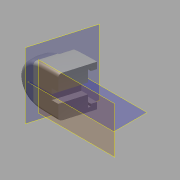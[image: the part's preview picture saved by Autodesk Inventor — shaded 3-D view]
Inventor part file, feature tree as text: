
AUTODESK INVENTOR PART (.ipt)
format: ipt  version: 2012 SP2 (Build 160219200, 219)  size: 716,288 bytes
history: native  units: in
note: dims shown in document units (in); Inventor stores cm internally (conversion verified against a paired STEP export)
features: sketch x21, sweep x7, extrude x5, plane x4, projected_geometry x3, fillet x2, other x2, mirror x1, surface_op x1
ambient origin geometry x8: Origin, YZ Plane, XZ Plane, XY Plane, X Axis, Y Axis, Z Axis, Center Point
bodies: Solid1 (feature_tree)
feature tree (46):
  sketch  "Sketch1"  dims[d6=0.9405in d9=0.688in]
  plane  "Work Plane1"
  plane  "Work Plane2"
  sketch  "Sketch3"  dims[d12=0.2381in d13=0.5734in]
  plane  "Work Plane3"
  sweep  "Sweep1"
  sweep  "Sweep2"
  extrude  "Extrusion1"  Depth=0.5734in
  plane  "Work Plane4"
  mirror  "Mirror1"
  sweep  "Sweep3"
  sweep  "Sweep5"
  sweep  "Sweep6"
  extrude  "Extrusion3"  Depth=0.7769in
  fillet  "Fillet2"  Radius=0.3374in
  fillet  "Fillet3"  Radius=0.1206in
  sweep  "Sweep8"
  sweep  "Sweep9"
  extrude  "Extrusion4"  Depth=0.9887in
  extrude  "Extrusion5"  Depth=1.1563in
  extrude  "Extrusion6"  Depth=1.2792in
  other  "Image1"
  sketch  "Sketch2"  dims[d10=0.069in d11=0.12in]
  other  "Srf1"
  sketch  "Sketch4"  dims[d14=0.4256in d15=1.588in]
  sketch  "Sketch5"  dims[d16=0.3503in d17=0.5806in]
  sketch  "Sketch6"  dims[d18=0.3426in d19=0.2058in]
  sketch  "Sketch7"  dims[d20=0.3395in d21=0.7769in d22=0.3374in d23=0.1206in]
  sketch  "Sketch8"  dims[d24=0.3329in d25=0.8673in]
  sketch  "Sketch9"  dims[d26=0.3313in d27=0.0621in]
  sketch  "Sketch10"  dims[d28=0.323in d29=0.9887in]
  sketch  "Sketch14"  dims[d30=0.2944in d31=1.1563in]
  sketch  "Sketch15"  dims[d32=0.2583in d33=1.2792in]
  sketch  "Sketch16"  dims[d34=0.1988in]
  sketch  "Sketch18"  dims[d35=1.391in]
  projected_geometry  "Projected Loop2"
  sketch  "Sketch20"  dims[d36=0.1269in]
  sketch  "3D Sketch2"
  sketch  "Sketch21"  dims[d37=1.4752in]
  sketch  "3D Sketch3"
  sketch  "Sketch22"  dims[d38=0.0171in]
  projected_geometry  "Projected Loop3"
  projected_geometry  "Projected Loop4"
  sketch  "Sketch23"  dims[d39=1.5524in]
  sketch  "Sketch24"  dims[d40=0.0519in d41=1.5805in d42=0.1042in d43=1.7561in d44=0.2965in d47=0.5902in d48=0.2in d49=0.0in d50=0.6495in d51=1.035in d52=0.5105in d53=0.306in d54=0.5955in d55=0.0in d56=0.6605in d57=0.053in d58=0.1095in d59=0.2in d60=0.055in d61=0.0in d62=0.7687in d64=0.3167in d65=0.4475in d66=0.0in d67=0.0285in d68=0.0285in d69=0.0285in d70=0.0285in d71=0.0285in d72=0.0285in d76=0.0in d77=0.0in d85=1.0in d86=0.0in d87=0.075in d88=0.075in d90=0.0in d91=0.0in d92=1.0in d93=0.0in d94=1.0in d95=0.0in d96=1.0in d97=0.0in]
  surface_op  "Boundary Patch1"
